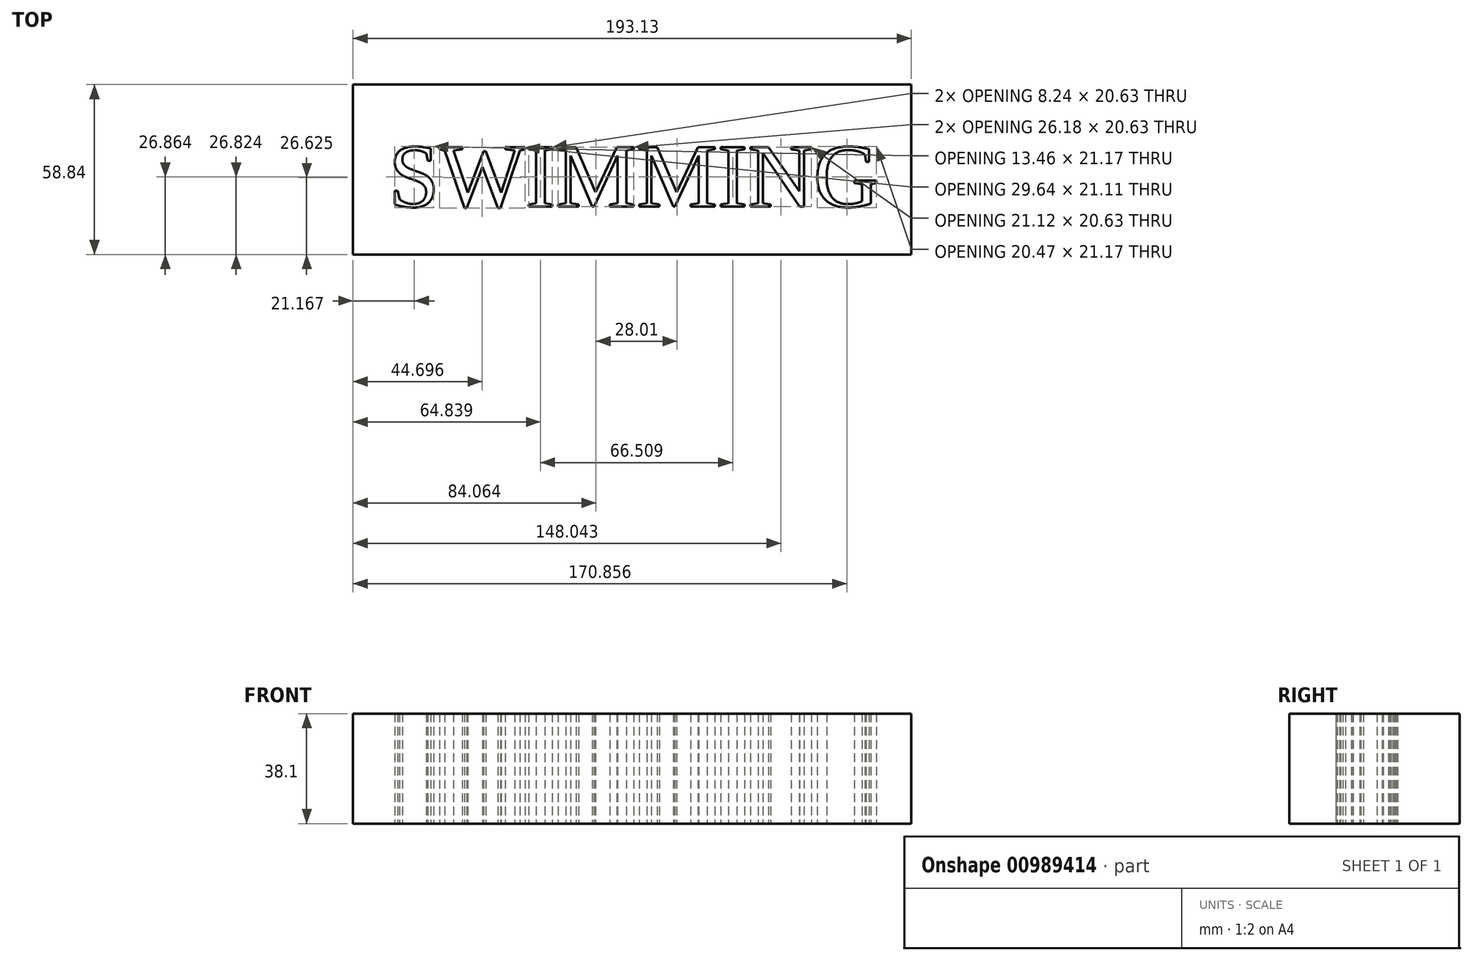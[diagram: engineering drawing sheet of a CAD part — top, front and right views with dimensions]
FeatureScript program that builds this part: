
annotation { "Feature Type Name" : "Feature", "Feature Type Description" : "" }
export const myFeature = defineFeature(function(context is Context, id is Id, definition is map)
    precondition{}
    {
        {
            var Q0;
            Q0=qCreatedBy(makeId("Top.planeOp"),FACE);
            var sketch = newSketch(context, id + "F0", { "sketchPlane" : qUnion([Q0])});
            skLineSegment(sketch, "E0.bottom", {"start": v(-89.96, 19.61) * mm, "end": v(103.17, 19.61) * mm});
            skLineSegment(sketch, "E0.top", {"start": v(-89.96, -39.23) * mm, "end": v(103.17, -39.23) * mm});
            skLineSegment(sketch, "E0.left", {"start": v(-89.96, 19.61) * mm, "end": v(-89.96, -39.23) * mm});
            skLineSegment(sketch, "E0.right", {"start": v(103.17, 19.61) * mm, "end": v(103.17, -39.23) * mm});
            skText(sketch, "E1", { "text": "SWIMMING", "fontName": "Tinos-Regular.ttf"});
            const initialGuessF0  = {"E1": [-0.07763, -0.02268, 1, 0, 0.02268]};
            skSetInitialGuess(sketch, initialGuessF0);
            skSolve(sketch);
        }
        {
            var Q0;
            Q0 = qSketchRegion(id + "F0", true);
            extrude(context, id + "F1", {"entities" : qUnion([Q0]), "depth" : 38.1 * mm, "offsetDistance" : 25.4 * mm});
        }
    });
